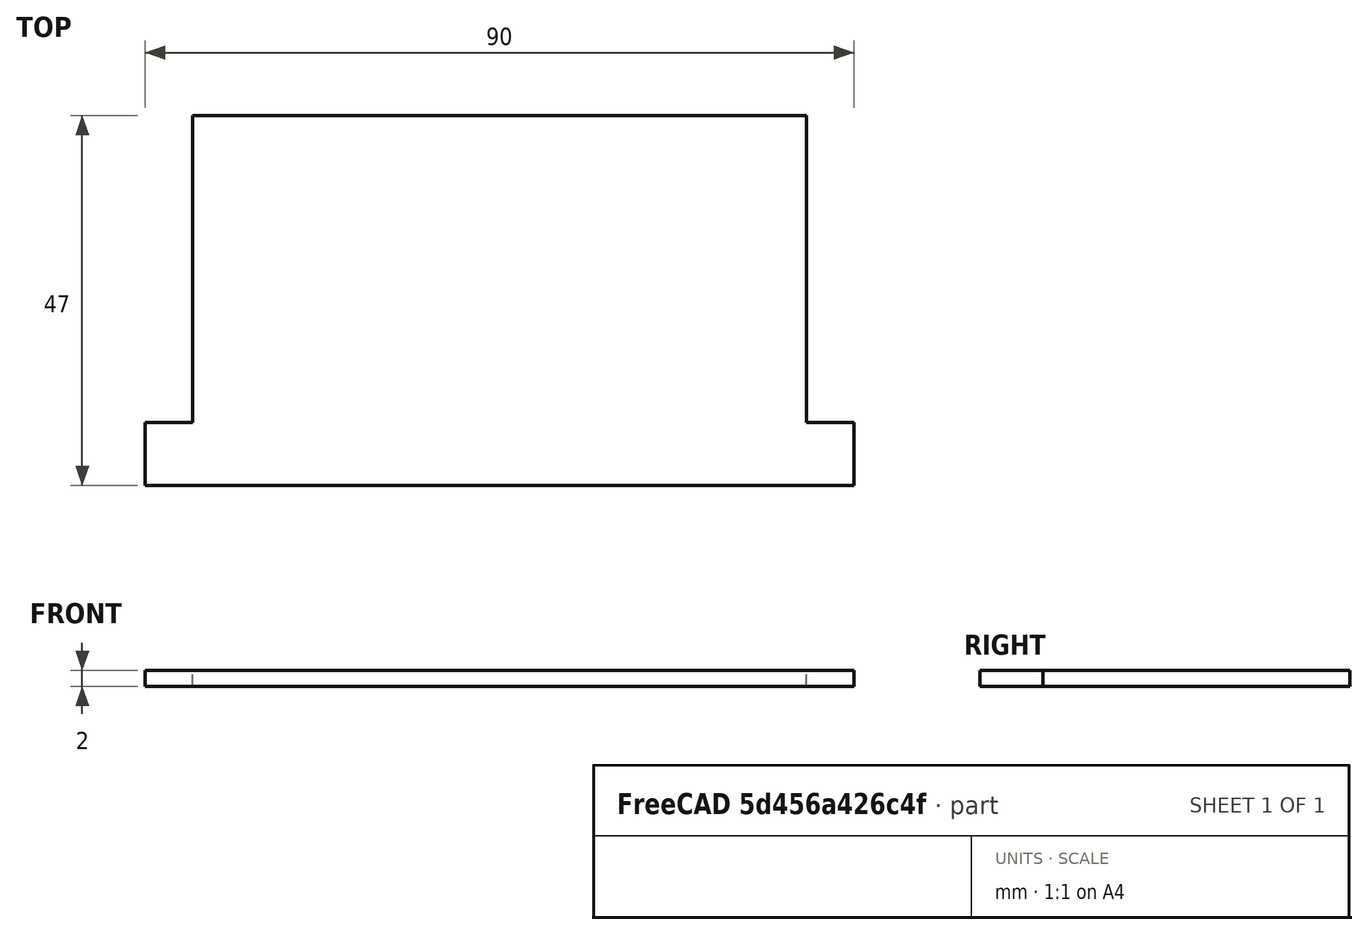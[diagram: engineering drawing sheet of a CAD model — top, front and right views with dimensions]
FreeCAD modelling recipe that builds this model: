
FCSTD DOCUMENT  (FreeCAD 1.0R39109 (Git))
Label: speaker_cover
License: All rights reserved
LicenseURL: https://en.wikipedia.org/wiki/All_rights_reserved
objects: PartDesign::ShapeBinder×1, Sketcher::SketchObject×1, PartDesign::Pad×1, PartDesign::Body×1
note: 7 computed .brp shape members not serialized (recipe doc carries the construction recipe); baked Part::Feature solids carry a one-line shape summary decoded from their .brp

FEATURE [PartDesign::ShapeBinder] CopyPad007
  TraceSupport = false
FEATURE [Sketcher::SketchObject] Sketch
  ArcFitTolerance = 1e-06
  AttachmentSupport = -> [CopyPad007]
  ExternalGeometry = -> [CopyPad007]
  FullyConstrained = true
  MakeInternals = false
  MapMode = 5
  Placement = pos=(0,0,82) rot=(0,0,1;0rad)
  sketch-geometry (8):
    g0: LineSegment StartX=15 StartY=4 StartZ=0 EndX=15 EndY=12 EndZ=0
    g1: LineSegment StartX=15 StartY=12 StartZ=0 EndX=21 EndY=12 EndZ=0
    g2: LineSegment StartX=21 StartY=12 StartZ=0 EndX=21 EndY=51 EndZ=0
    g3: LineSegment StartX=21 StartY=51 StartZ=0 EndX=99 EndY=51 EndZ=0
    g4: LineSegment StartX=99 StartY=51 StartZ=0 EndX=99 EndY=12 EndZ=0
    g5: LineSegment StartX=99 StartY=12 StartZ=0 EndX=105 EndY=12 EndZ=0
    g6: LineSegment StartX=105 StartY=12 StartZ=0 EndX=105 EndY=4 EndZ=0
    g7: LineSegment StartX=105 StartY=4 StartZ=0 EndX=15 EndY=4 EndZ=0
  constraints (16):
    c: Coincident(g-6,g0)
    c: Coincident(g0,g-5)
    c: Coincident(g0,g1)
    c: Coincident(g1,g-5)
    c: Coincident(g1,g2)
    c: Coincident(g2,g-13)
    c: Coincident(g2,g3)
    c: Coincident(g3,g-13)
    c: Coincident(g3,g4)
    c: Coincident(g4,g-18)
    c: Coincident(g4,g5)
    c: Coincident(g5,g-18)
    c: Coincident(g5,g6)
    c: Coincident(g6,g-17)
    c: Coincident(g6,g7)
    c: Coincident(g7,g0)
FEATURE [PartDesign::Pad] Pad
  Direction = (0,0,1)
  Length = 2
  Length2 = 10
  Profile = -> Sketch
  ReferenceAxis = -> Sketch [N_Axis]
  Refine = true
  Suppressed = false
  Type = 0
  expr: Length = 2 mm
FEATURE [PartDesign::Body] Body001  label="speaker_cover"
  AllowCompound = false
  Group = -> [CopyPad007,Sketch,Pad]
  Origin = -> Origin001
  Placement = pos=(7.38659,4.95915,2.14746) rot=(0,0,1;0rad)
  Tip = -> Pad
